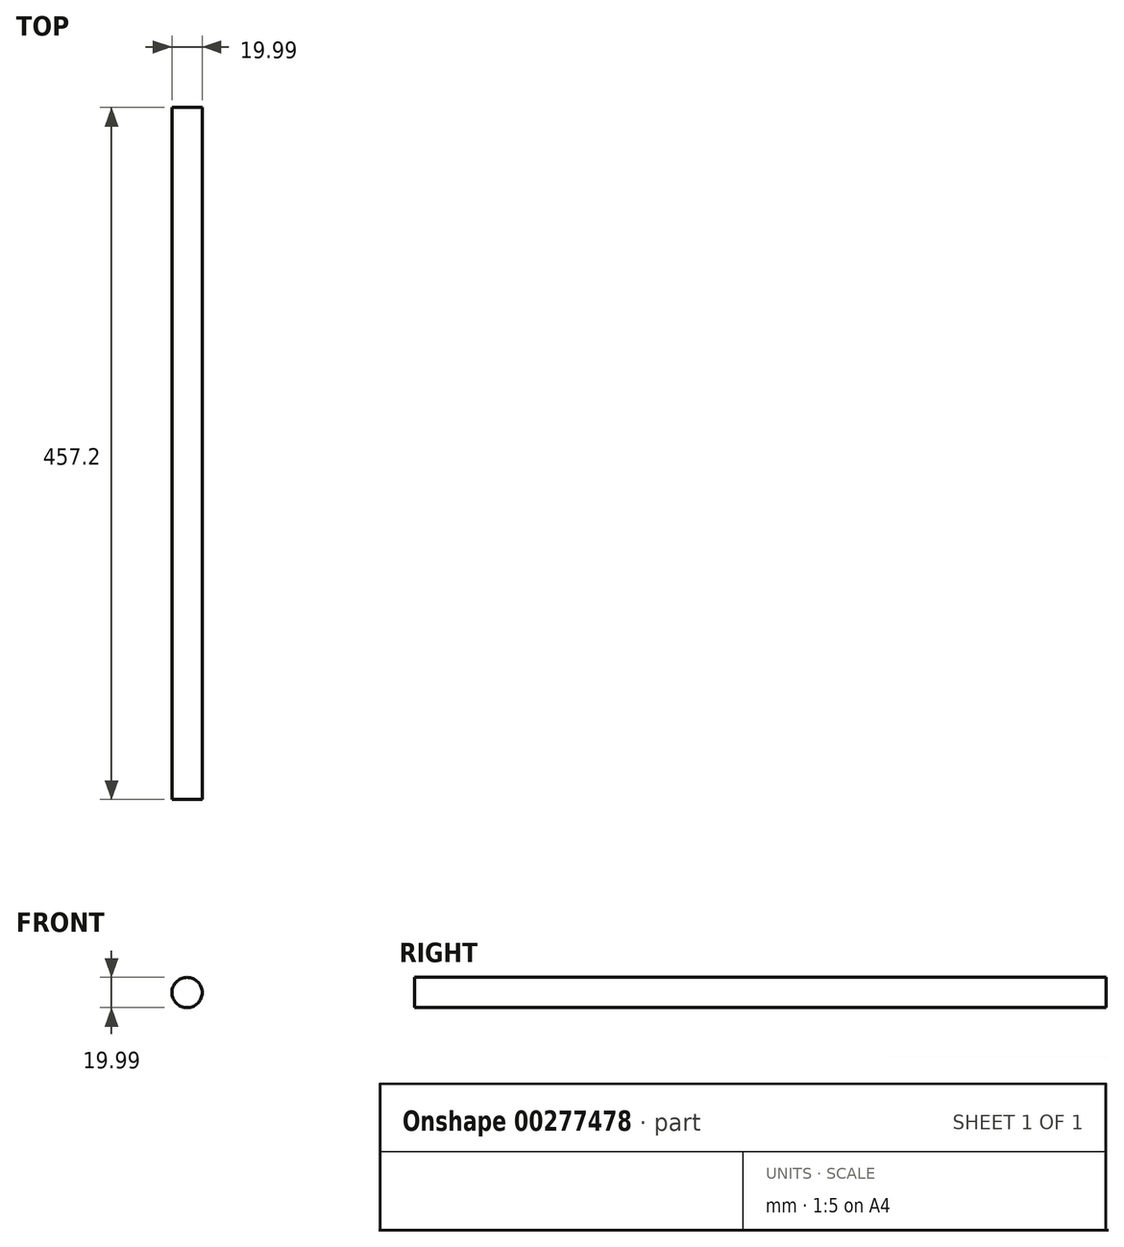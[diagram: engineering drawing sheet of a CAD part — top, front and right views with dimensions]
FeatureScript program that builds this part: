
annotation { "Feature Type Name" : "Feature", "Feature Type Description" : "" }
export const myFeature = defineFeature(function(context is Context, id is Id, definition is map)
    precondition{}
    {
        {
            var Q0;
            Q0=qCreatedBy(makeId("Front.planeOp"),FACE);
            var sketch = newSketch(context, id + "F0", { "sketchPlane" : qUnion([Q0])});
            skCircle(sketch, "E0", {"center": v(-19.28, 13.15) * mm, "radius": 10 * mm});
            skSolve(sketch);
        }
        {
            var Q0;
            Q0 = qSketchRegion(id + "F0", true);
            extrude(context, id + "F1", {"entities" : qUnion([Q0]), "depth" : 457.2 * mm});
        }
    });
